# Revit family: Mirac LED 2-line - Generic
name_source: partatom
category: Lighting Fixtures
revit_build: Autodesk Revit Architecture 2014 (Build: 20140709_2115(x64)
units: mm (PartAtom-declared; Revit-internal decimal feet)

## types (4) — shared parameters
Apparent Load = 240 VA
ArticleNumber = See URL hyperlink
AssetType = Moveable/Fixed
BSAB 96 = SNB.2
BallastsCELMAEnergyEfficiencyIndex = Class A1/A2
CCSClassCode = UAC
CCSClassName = Belysningsarmatur
CCSTopnode = L
Cassette = Riegens_Steel_Powder coated white RAL901025
Cassette Depth = 570 mm
Cassette Thickness = 59 mm
Cassette Width = 547 mm
Clearance Zones = Yes
Clearance Zones Offset = 60 mm
Colour = White
ControlGearPosition = Integrated
Description = 70-80-35 General Lighting Systems
DocumentReference = See URL hyperlink
Documentation = See URL hyperlink
Finish = Powder coated
Frame = Riegens_Steel_Powder coated white RAL901025
Frame Thickness = 9 mm
Glass Thickness = 2 mm
HasProtectiveEarth = TRUE
IP_Code = IP20
IfcExportAs = IfcLightFixtureType'
IfcExportType = NOTDEFINED'
InsulationStandardClass = Class 1
InternalFuse = Only required in emergency versions
LampColourRenderingIndex = Ra>80
LampRating = 21W
LampType = LED
Light Source Definition (family) = Point+HemiSpherical
LightFixtureMountingType = Recessed
LightFixturePlacingType = Ceiling
LightSource = LED 3000K / 4000K
LuminairePowerFactor = >0,9
LuminaireType = Recessed Direct LED Luminaire
Manufacturer = Riegens A/S
ManufacturerURL = www.riegens.com
Material = Steel and louvre in Miro finish
NominalVoltage = 220-240V
OmniClass Number = 23.80.70.11
OmniClass Title = Luminaries for Internal Lighting
Optic = Satin-matt double parabolic louvre
PhaseReference = IEC recommendations
PhotometricPerformance = In accordance with BS EN 13032-1
ProductInformation = http://riegens.com
Shape = Square
TotalWattage = Max. 24W
URL = http://riegens.com
Uniclass 1.4 = JY73
Uniclass2 = Pr_70_70_49_43 Light-Emitting Diode (LED) Luminaires
Version = v.1.0

## per-type parameters (varying)
| type | BIMObjectName | Frame Depth | Frame Width | Model | ModelReference | Size |
| Mirac LED 2-line 600x600 C | Mirac LED 2-line 600x600 C.rfa | 622 mm | 622 mm | Mirac LED 2-line 600x600 C | Mirac LED 2-line 600x600 C | 600 x 600 mm |
| Mirac LED 2-line 600x600 T/L | Mirac LED 2-line 600x600 T/L.rfa | 595 mm | 595 mm | Mirac LED 2-line 600x600 T/L | Mirac LED 2-line 600x600 T/L | 600 x 600 mm |
| Mirac LED 2-line 625x625 T/L/C | Mirac LED 2-line 600x600 T/L/C.rfa | 622 mm | 622 mm | Mirac LED 2-line 600x600 T/L/C | Mirac LED 2-line 600x600 T/L/C | 625 x 625 mm |
| Mirac LED 2-line 600x600 SAS | Mirac LED 2-line 600x600 SAS.rfa | 584 mm | 584 mm | Mirac LED 2-line 600x600 SAS | Mirac LED 2-line 600x600 SAS | 600 x 600 mm |

## geometry (parser evidence)
native form markers: Sweep x2
no freeform markers — native parametric forms only
